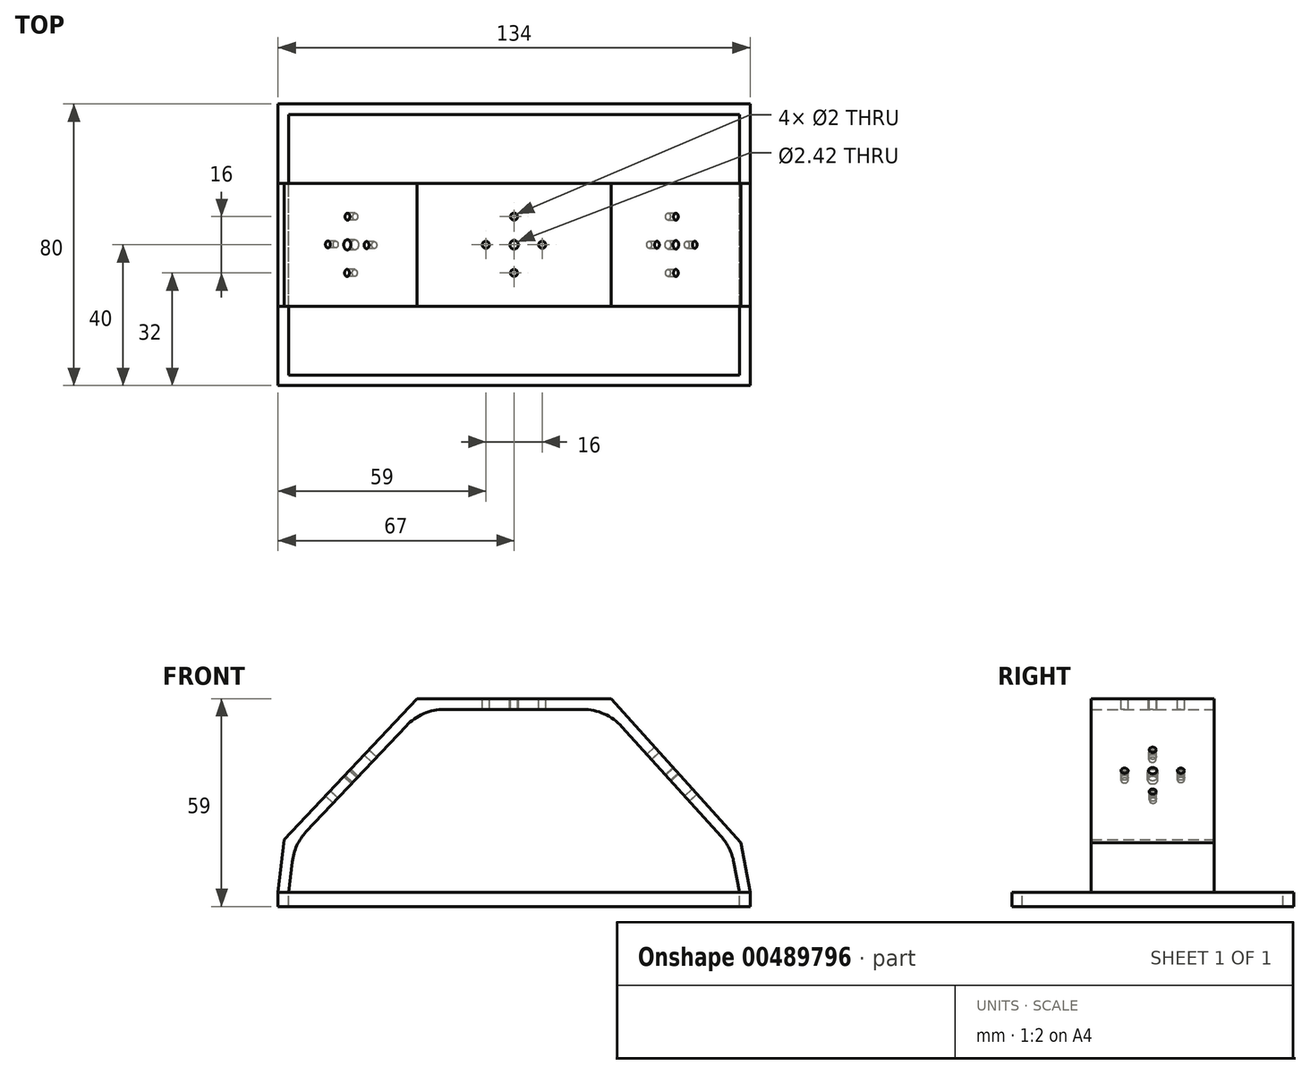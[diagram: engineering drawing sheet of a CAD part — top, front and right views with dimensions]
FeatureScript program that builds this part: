
annotation { "Feature Type Name" : "Feature", "Feature Type Description" : "" }
export const myFeature = defineFeature(function(context is Context, id is Id, definition is map)
    precondition{}
    {
        {
            var Q0;
            Q0=qCreatedBy(makeId("Top.planeOp"),FACE);
            var sketch = newSketch(context, id + "F0", { "sketchPlane" : qUnion([Q0])});
            skLineSegment(sketch, "E0.bottom", {"start": v(-67, 40) * mm, "end": v(67, 40) * mm});
            skLineSegment(sketch, "E0.top", {"start": v(-67, -40) * mm, "end": v(67, -40) * mm});
            skLineSegment(sketch, "E0.left", {"start": v(-67, 40) * mm, "end": v(-67, -40) * mm});
            skLineSegment(sketch, "E0.right", {"start": v(67, 40) * mm, "end": v(67, -40) * mm});
            skSolve(sketch);
        }
        {
            var Q0;
            Q0=makeQuery(id+"F0.imprint","IMPRINT",FACE,{"disambiguationData":[TD([[makeQuery(id+"F0.imprint","IMPRINT",EDGE,{"derivedFrom":sQuery(id+"F0.wireOp",EDGE,"E0.bottom")}),-1.0]])]});
            extrude(context, id + "F1", {"entities" : qUnion([Q0]), "depth" : 4 * mm});
        }
        {
            var Q0;
            Q0=makeQuery(id+"F1.opExtrude","CAP_FACE",FACE,{"disambiguationData":[OSD([sQuery(id+"F0.wireOp",EDGE,"E0.bottom"),sQuery(id+"F0.wireOp",EDGE,"E0.top"),sQuery(id+"F0.wireOp",EDGE,"E0.left"),sQuery(id+"F0.wireOp",EDGE,"E0.right")])],"isStart":true});
            var sketch = newSketch(context, id + "F2", { "sketchPlane" : qUnion([Q0])});
            skLineSegment(sketch, "E1.bottom", {"start": v(-64, 37) * mm, "end": v(64, 37) * mm});
            skLineSegment(sketch, "E1.top", {"start": v(-64, -37) * mm, "end": v(64, -37) * mm});
            skLineSegment(sketch, "E1.left", {"start": v(-64, 37) * mm, "end": v(-64, -37) * mm});
            skLineSegment(sketch, "E1.right", {"start": v(64, 37) * mm, "end": v(64, -37) * mm});
            skLineSegment(sketch, "E2.bottom", {"start": v(-61, 34) * mm, "end": v(61, 34) * mm});
            skLineSegment(sketch, "E2.top", {"start": v(-61, -34) * mm, "end": v(61, -34) * mm});
            skLineSegment(sketch, "E2.left", {"start": v(-61, 34) * mm, "end": v(-61, -34) * mm});
            skLineSegment(sketch, "E2.right", {"start": v(61, 34) * mm, "end": v(61, -34) * mm});
            skSolve(sketch);
        }
        {
            var Q0;
            Q0=makeQuery(id+"F2.imprint","IMPRINT",FACE,{"disambiguationData":[TD([[makeQuery(id+"F2.imprint","IMPRINT",EDGE,{"derivedFrom":sQuery(id+"F2.wireOp",EDGE,"E1.bottom")}),-1.0]])]});
            var Q1;
            Q1=makeQuery(id+"F2.imprint","IMPRINT",FACE,{"disambiguationData":[TD([[makeQuery(id+"F2.imprint","IMPRINT",EDGE,{"derivedFrom":sQuery(id+"F2.wireOp",EDGE,"E2.bottom")}),-1.0]])]});
            extrude(context, id + "F3", {"entities" : qUnion([Q0, Q1]), "operationType" : NewBodyOperationType.REMOVE, "depth" : 2 * mm, "hasSecondDirection" : true, "secondDirectionOppositeDirection" : true, "secondDirectionDepth" : 4 * mm});
        }
        {
            var Q0;
            Q0=qCreatedBy(makeId("Front.planeOp"),FACE);
            var sketch = newSketch(context, id + "F4", { "sketchPlane" : qUnion([Q0])});
            skLineSegment(sketch, "E3", {"start": v(-65.24, 18.99) * mm, "end": v(-27.5, 59) * mm});
            skLineSegment(sketch, "E4", {"start": v(-27.5, 59) * mm, "end": v(27.5, 59) * mm});
            skLineSegment(sketch, "E5", {"start": v(27.5, 59) * mm, "end": v(64.35, 18.17) * mm});
            skLineSegment(sketch, "E6", {"start": v(-65.24, 18.99) * mm, "end": v(-67, 4) * mm});
            skLineSegment(sketch, "E7", {"start": v(64.35, 18.17) * mm, "end": v(67, 4) * mm});
            skLineSegment(sketch, "E8", {"start": v(67, 4) * mm, "end": v(64, 4) * mm});
            skLineSegment(sketch, "E9", {"start": v(64, 4) * mm, "end": v(61.62, 16.71) * mm});
            skLineSegment(sketch, "E10", {"start": v(61.62, 16.71) * mm, "end": v(26.17, 56) * mm});
            skLineSegment(sketch, "E11", {"start": v(26.17, 56) * mm, "end": v(-26.2, 56) * mm});
            skLineSegment(sketch, "E12", {"start": v(-26.2, 56) * mm, "end": v(-62.4, 17.63) * mm});
            skLineSegment(sketch, "E13", {"start": v(-62.4, 17.63) * mm, "end": v(-64, 4) * mm});
            skLineSegment(sketch, "E14", {"start": v(-64, 4) * mm, "end": v(-67, 4) * mm});
            skSolve(sketch);
        }
        {
            var Q0;
            Q0=qSketchRegion(id+"F4",true);
            extrude(context, id + "F5", {"entities" : qUnion([Q0]), "operationType" : NewBodyOperationType.ADD, "endBound" : BoundingType.SYMMETRIC, "depth" : 35 * mm});
        }
        {
            var Q0;
            Q0=makeQuery(id+"F5.opExtrude","SWEPT_FACE",FACE,{"disambiguationData":[OSD([sQuery(id+"F4.wireOp",EDGE,"E4")])]});
            var sketch = newSketch(context, id + "F6", { "sketchPlane" : qUnion([Q0])});
            skCircle(sketch, "E15", {"center": v(0, 0) * mm, "radius": 1.21 * mm});
            skCircle(sketch, "E16", {"center": v(-8, 0) * mm, "radius": 1 * mm});
            skCircle(sketch, "E17.1.0", {"center": v(0, -8) * mm, "radius": 1 * mm});
            skCircle(sketch, "E17.2.0", {"center": v(8, 0) * mm, "radius": 1 * mm});
            skCircle(sketch, "E17.3.0", {"center": v(0, 8) * mm, "radius": 1 * mm});
            skSolve(sketch);
        }
        {
            var Q0;
            Q0=makeQuery(id+"F5.opExtrude","SWEPT_FACE",FACE,{"disambiguationData":[OSD([sQuery(id+"F4.wireOp",EDGE,"E3")])]});
            var sketch = newSketch(context, id + "F7", { "sketchPlane" : qUnion([Q0])});
            skCircle(sketch, "E18", {"center": v(0, -4.9) * mm, "radius": 1.46 * mm});
            skCircle(sketch, "E19", {"center": v(-8, -4.8) * mm, "radius": 1 * mm});
            skCircle(sketch, "E20.1.0", {"center": v(-0.1, -12.9) * mm, "radius": 1 * mm});
            skCircle(sketch, "E20.2.0", {"center": v(8, -5) * mm, "radius": 1 * mm});
            skCircle(sketch, "E20.3.0", {"center": v(0.1, 3.1) * mm, "radius": 1 * mm});
            skSolve(sketch);
        }
        {
            var Q0;
            Q0=makeQuery(id+"F5.opExtrude","SWEPT_FACE",FACE,{"disambiguationData":[OSD([sQuery(id+"F4.wireOp",EDGE,"E5")])]});
            var sketch = newSketch(context, id + "F8", { "sketchPlane" : qUnion([Q0])});
            skCircle(sketch, "E21", {"center": v(0, -2.12) * mm, "radius": 1.21 * mm});
            skCircle(sketch, "E22", {"center": v(-8, -2.12) * mm, "radius": 1 * mm});
            skCircle(sketch, "E23.1.0", {"center": v(0, -10.12) * mm, "radius": 1 * mm});
            skCircle(sketch, "E23.2.0", {"center": v(8, -2.12) * mm, "radius": 1 * mm});
            skCircle(sketch, "E23.3.0", {"center": v(0, 5.88) * mm, "radius": 1 * mm});
            skSolve(sketch);
        }
        {
            var Q0;
            Q0=qSketchRegion(id+"F6",true);
            extrude(context, id + "F9", {"entities" : qUnion([Q0]), "operationType" : NewBodyOperationType.REMOVE, "oppositeDirection" : true, "depth" : 25 * mm});
        }
        {
            var Q0;
            Q0=qSketchRegion(id+"F7",true);
            extrude(context, id + "F10", {"entities" : qUnion([Q0]), "operationType" : NewBodyOperationType.REMOVE, "oppositeDirection" : true, "depth" : 25 * mm});
        }
        {
            var Q0;
            Q0=qSketchRegion(id+"F8",true);
            extrude(context, id + "F11", {"entities" : qUnion([Q0]), "operationType" : NewBodyOperationType.REMOVE, "oppositeDirection" : true, "depth" : 25 * mm});
        }
        {
            var Q0;
            Q0=makeQuery(id+"F5.opExtrude","SWEPT_EDGE",EDGE,{"disambiguationData":[OSD([sQuery(id+"F4.wireOp",EDGE,"E10"),sQuery(id+"F4.wireOp",EDGE,"E11")])]});
            var Q1;
            Q1=makeQuery(id+"F5.opExtrude","SWEPT_EDGE",EDGE,{"disambiguationData":[OSD([sQuery(id+"F4.wireOp",EDGE,"E11"),sQuery(id+"F4.wireOp",EDGE,"E12")])]});
            var Q2;
            Q2=makeQuery(id+"F5.opExtrude","SWEPT_EDGE",EDGE,{"disambiguationData":[OSD([sQuery(id+"F4.wireOp",EDGE,"E9"),sQuery(id+"F4.wireOp",EDGE,"E10")])]});
            var Q3;
            Q3=makeQuery(id+"F5.opExtrude","SWEPT_EDGE",EDGE,{"disambiguationData":[OSD([sQuery(id+"F4.wireOp",EDGE,"E12"),sQuery(id+"F4.wireOp",EDGE,"E13")])]});
            fillet(context, id + "F12", {"entities" : qUnion([Q0, Q1, Q2, Q3]), "radius" : 15 * mm, "tangentPropagation" : true, "allowEdgeOverflow" : false});
        }
    });
